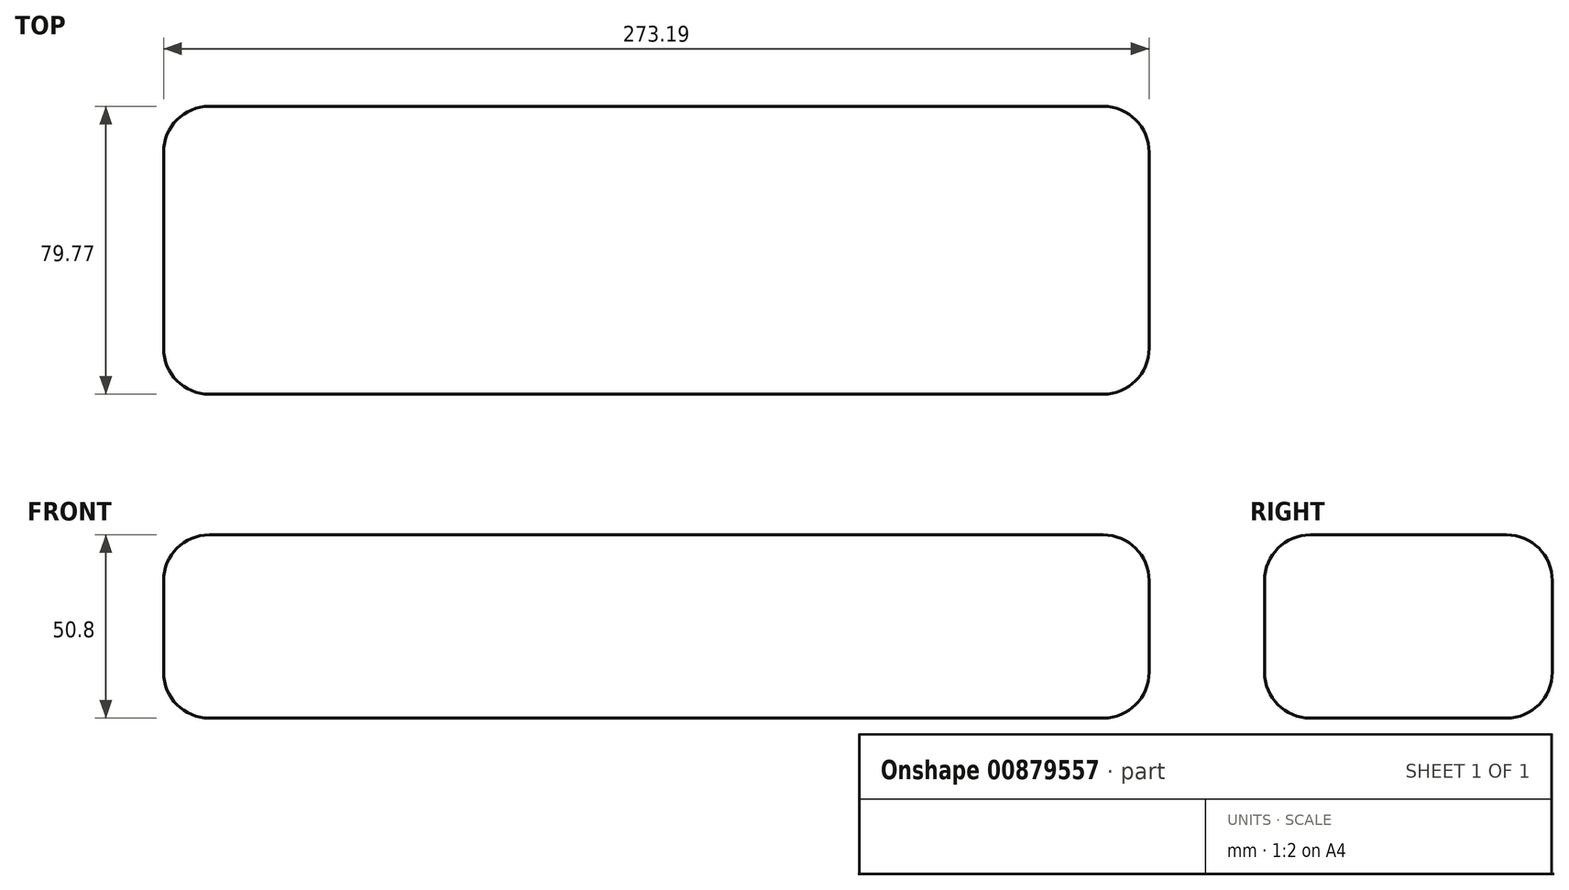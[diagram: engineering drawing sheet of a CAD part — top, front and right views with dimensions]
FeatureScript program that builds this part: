
annotation { "Feature Type Name" : "Feature", "Feature Type Description" : "" }
export const myFeature = defineFeature(function(context is Context, id is Id, definition is map)
    precondition{}
    {
        {
            var Q0;
            Q0=qCreatedBy(makeId("Top.planeOp"),FACE);
            var sketch = newSketch(context, id + "F0", { "sketchPlane" : qUnion([Q0])});
            skLineSegment(sketch, "E0.bottom", {"start": v(-114.56, -10.11) * mm, "end": v(158.63, -10.11) * mm});
            skLineSegment(sketch, "E0.top", {"start": v(-114.56, -89.88) * mm, "end": v(158.63, -89.88) * mm});
            skLineSegment(sketch, "E0.left", {"start": v(-114.56, -10.11) * mm, "end": v(-114.56, -89.88) * mm});
            skLineSegment(sketch, "E0.right", {"start": v(158.63, -10.11) * mm, "end": v(158.63, -89.88) * mm});
            skSolve(sketch);
        }
        {
            var Q0;
            Q0 = qSketchRegion(id + "F0", true);
            extrude(context, id + "F1", {"entities" : qUnion([Q0]), "depth" : 50.8 * mm, "offsetDistance" : 25.4 * mm});
        }
        {
            var Q0;
            Q0=makeQuery(id+"F1.opExtrude","CAP_EDGE",EDGE,{"disambiguationData":[OSD([sQuery(id+"F0.wireOp",EDGE,"E0.top")])],"isStart":false});
            var Q1;
            Q1=makeQuery(id+"F1.opExtrude","CAP_EDGE",EDGE,{"disambiguationData":[OSD([sQuery(id+"F0.wireOp",EDGE,"E0.left")])],"isStart":false});
            var Q2;
            Q2=makeQuery(id+"F1.opExtrude","CAP_EDGE",EDGE,{"disambiguationData":[OSD([sQuery(id+"F0.wireOp",EDGE,"E0.bottom")])],"isStart":false});
            var Q3;
            Q3=makeQuery(id+"F1.opExtrude","CAP_EDGE",EDGE,{"disambiguationData":[OSD([sQuery(id+"F0.wireOp",EDGE,"E0.right")])],"isStart":false});
            var Q4;
            Q4=makeQuery(id+"F1.opExtrude","CAP_EDGE",EDGE,{"disambiguationData":[OSD([sQuery(id+"F0.wireOp",EDGE,"E0.right")])],"isStart":true});
            var Q5;
            Q5=makeQuery(id+"F1.opExtrude","SWEPT_FACE",FACE,{"disambiguationData":[OSD([sQuery(id+"F0.wireOp",EDGE,"E0.top")])]});
            var Q6;
            Q6=makeQuery(id+"F1.opExtrude","CAP_EDGE",EDGE,{"disambiguationData":[OSD([sQuery(id+"F0.wireOp",EDGE,"E0.bottom")])],"isStart":true});
            var Q7;
            Q7=makeQuery(id+"F1.opExtrude","SWEPT_FACE",FACE,{"disambiguationData":[OSD([sQuery(id+"F0.wireOp",EDGE,"E0.left")])]});
            fillet(context, id + "F2", {"entities" : qUnion([Q0, Q1, Q2, Q3, Q4, Q5, Q6, Q7]), "radius" : 12.7 * mm, "tangentPropagation" : true, "allowEdgeOverflow" : false});
        }
        {
            var Q0;
            Q0=makeQuery(id+"F1.opExtrude","SWEPT_EDGE",EDGE,{"disambiguationData":[OSD([sQuery(id+"F0.wireOp",EDGE,"E0.bottom"),sQuery(id+"F0.wireOp",EDGE,"E0.right")])]});
            fillet(context, id + "F3", {"entities" : qUnion([Q0]), "radius" : 12.7 * mm, "tangentPropagation" : true, "allowEdgeOverflow" : false});
        }
    });
